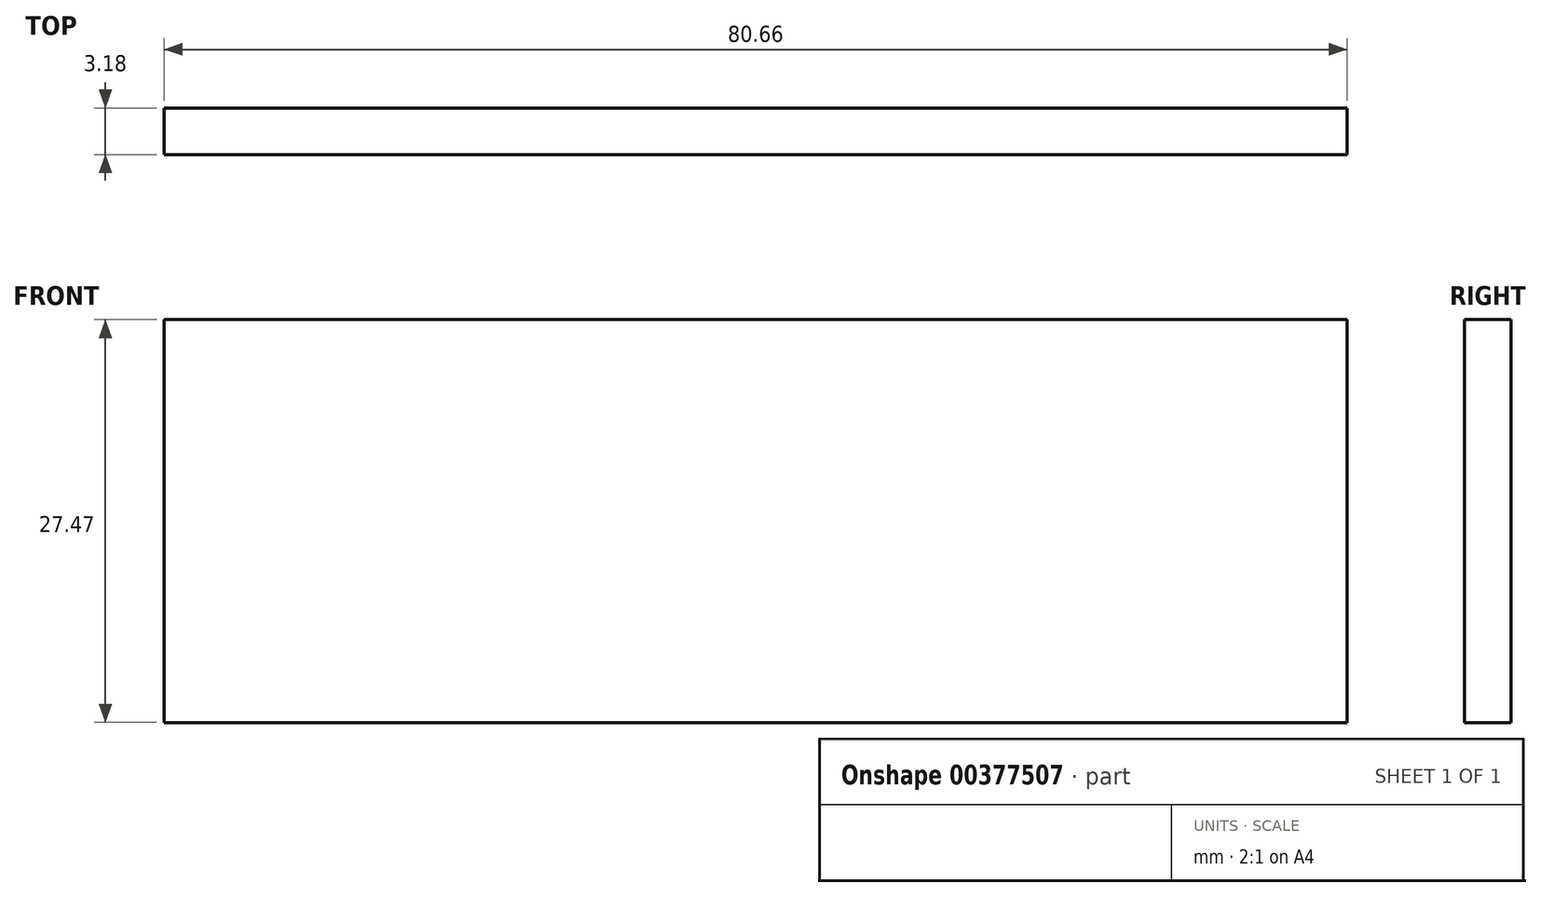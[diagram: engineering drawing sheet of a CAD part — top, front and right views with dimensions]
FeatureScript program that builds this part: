
annotation { "Feature Type Name" : "Feature", "Feature Type Description" : "" }
export const myFeature = defineFeature(function(context is Context, id is Id, definition is map)
    precondition{}
    {
        {
            var Q0;
            Q0=qCreatedBy(makeId("Front.planeOp"),FACE);
            var sketch = newSketch(context, id + "F0", { "sketchPlane" : qUnion([Q0])});
            skLineSegment(sketch, "E0.bottom", {"start": v(-14.89, 13.67) * mm, "end": v(65.77, 13.67) * mm});
            skLineSegment(sketch, "E0.top", {"start": v(-14.89, -13.8) * mm, "end": v(65.77, -13.8) * mm});
            skLineSegment(sketch, "E0.left", {"start": v(-14.89, 13.67) * mm, "end": v(-14.89, -13.8) * mm});
            skLineSegment(sketch, "E0.right", {"start": v(65.77, 13.67) * mm, "end": v(65.77, -13.8) * mm});
            skSolve(sketch);
        }
        {
            var Q0;
            Q0 = qSketchRegion(id + "F0", true);
            extrude(context, id + "F1", {"entities" : qUnion([Q0]), "endBound" : BoundingType.SYMMETRIC, "depth" : 3.17 * mm});
        }
    });
